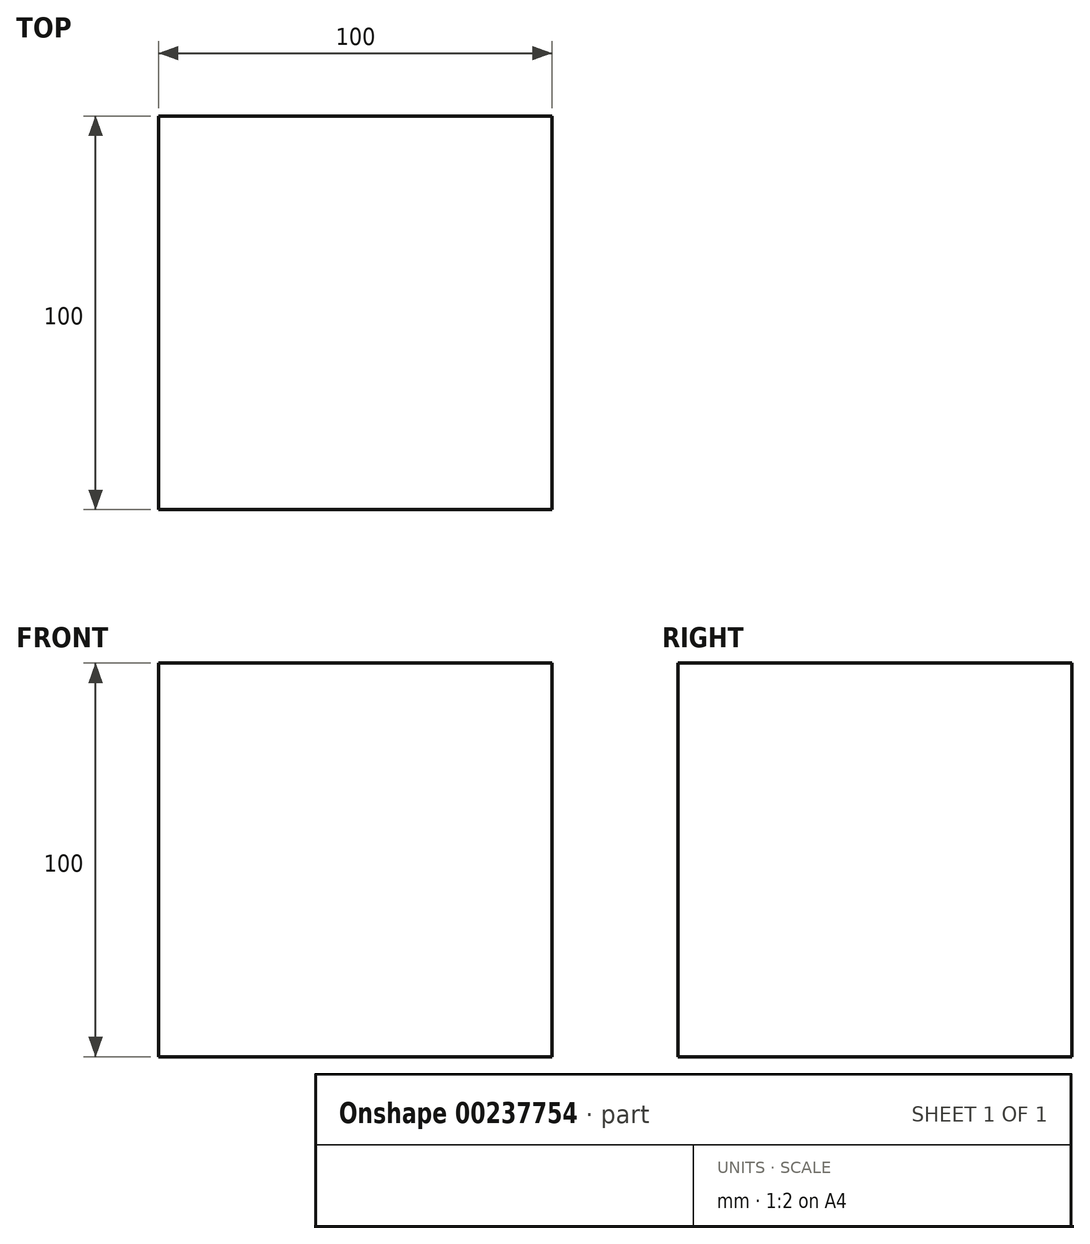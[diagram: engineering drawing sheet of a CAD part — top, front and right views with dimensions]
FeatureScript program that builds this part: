
annotation { "Feature Type Name" : "Feature", "Feature Type Description" : "" }
export const myFeature = defineFeature(function(context is Context, id is Id, definition is map)
    precondition{}
    {
        {
            var Q0;
            Q0=qCreatedBy(makeId("Top.planeOp"),FACE);
            var sketch = newSketch(context, id + "F0", { "sketchPlane" : qUnion([Q0])});
            skLineSegment(sketch, "E0.bottom", {"start": v(-200.43, -51.51) * mm, "end": v(-100.43, -51.51) * mm});
            skLineSegment(sketch, "E0.top", {"start": v(-200.43, -151.51) * mm, "end": v(-100.43, -151.51) * mm});
            skLineSegment(sketch, "E0.left", {"start": v(-200.43, -51.51) * mm, "end": v(-200.43, -151.51) * mm});
            skLineSegment(sketch, "E0.right", {"start": v(-100.43, -51.51) * mm, "end": v(-100.43, -151.51) * mm});
            skSolve(sketch);
        }
        {
            var Q0;
            Q0 = qSketchRegion(id + "F0", true);
            extrude(context, id + "F1", {"entities" : qUnion([Q0]), "depth" : 100 * mm});
        }
    });
